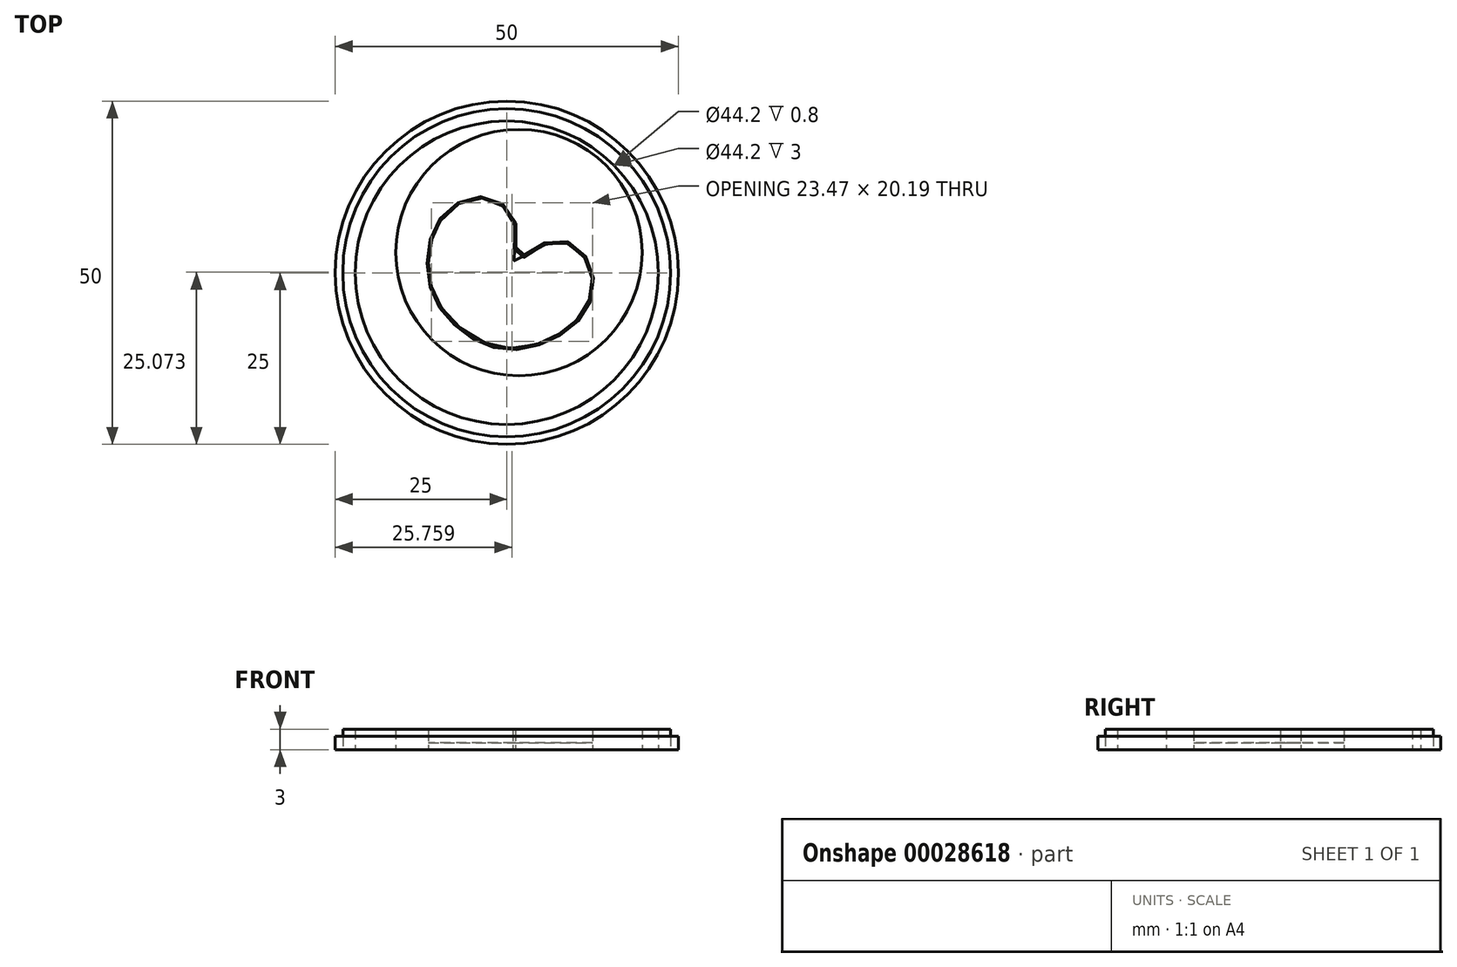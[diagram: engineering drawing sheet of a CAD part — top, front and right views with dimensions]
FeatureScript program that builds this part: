
annotation { "Feature Type Name" : "Feature", "Feature Type Description" : "" }
export const myFeature = defineFeature(function(context is Context, id is Id, definition is map)
    precondition{}
    {
        {
            var Q0;
            Q0=qCreatedBy(makeId("Top.planeOp"),FACE);
            var sketch = newSketch(context, id + "F0", { "sketchPlane" : qUnion([Q0])});
            skCircle(sketch, "E0", {"center": v(0, 0) * mm, "radius": 25 * mm});
            skCircle(sketch, "E1", {"center": v(0, 0) * mm, "radius": 23.9 * mm});
            skCircle(sketch, "E2", {"center": v(0, 0) * mm, "radius": 22.1 * mm});
            skCircle(sketch, "E3", {"center": v(1.78, 2.94) * mm, "radius": 17.95 * mm});
            skPoint(sketch, "E4", {"position": v(0, 25) * mm});
            skPoint(sketch, "E5", {"position": v(0, 20.8) * mm});
            skPoint(sketch, "E6", {"position": v(-15.93, 0) * mm});
            skPoint(sketch, "E7", {"position": v(-25, 0) * mm});
            skLineSegment(sketch, "E8", {"start": v(0.34, 31.79) * mm, "end": v(0.34, -39.78) * mm, "construction": true});
            skPoint(sketch, "E9", {"position": v(0.34, 0) * mm});
            skPoint(sketch, "E10", {"position": v(-3.9, 10.89) * mm});
            skPoint(sketch, "E11", {"position": v(12.51, -1.48) * mm});
            skPoint(sketch, "E12", {"position": v(0.65, -11.01) * mm});
            skPoint(sketch, "E13", {"position": v(-11.43, 1.18) * mm});
            skFitSpline(sketch, "E14", {"points": [v(-10.98, -2) * mm, v(-11.37, -0.01) * mm, v(-11.4, 1.98) * mm, v(-11.15, 3.98) * mm, v(-10.56, 5.9) * mm, v(-10.17, 6.73) * mm, v(-9.73, 7.55) * mm, v(-8.59, 8.96) * mm, v(-6.33, 10.35) * mm, v(-4.5, 10.86) * mm, v(-2.83, 10.77) * mm, v(-1.23, 10.17) * mm, v(0.23, 9.1) * mm, v(0.95, 7.82) * mm, v(1.27, 6.13) * mm, v(1.18, 4) * mm, v(0.99, 2.8) * mm, v(0.86, 2.24) * mm, v(0.93, 1.94) * mm, v(1.1, 1.73) * mm, v(1.55, 1.62) * mm, v(1.95, 1.8) * mm, v(3.45, 2.98) * mm, v(4.68, 3.75) * mm, v(6.04, 4.35) * mm, v(7.5, 4.61) * mm, v(8.89, 4.32) * mm, v(10.24, 3.45) * mm, v(11.54, 2.03) * mm, v(12.21, 0.64) * mm, v(12.5, -1.02) * mm, v(12.48, -2.05) * mm, v(12.07, -3.85) * mm, v(11.28, -5.48) * mm, v(10.26, -6.9) * mm, v(8.96, -8.07) * mm, v(7.48, -9.04) * mm, v(5.93, -9.85) * mm, v(2.94, -10.82) * mm, v(0.92, -11) * mm, v(-1.1, -10.87) * mm, v(-3.45, -10.13) * mm, v(-5.61, -8.95) * mm, v(-8.2, -6.79) * mm, v(-9.57, -5.06) * mm, v(-10.6, -3.07) * mm, v(-10.98, -2) * mm]});
            skLineSegment(sketch, "E15", {"start": v(-11.43, 18.63) * mm, "end": v(-11.43, -20.08) * mm, "construction": true});
            skLineSegment(sketch, "E16", {"start": v(-26.76, 10.89) * mm, "end": v(26.59, 10.89) * mm, "construction": true});
            skLineSegment(sketch, "E17", {"start": v(12.51, 19.74) * mm, "end": v(12.51, -18.58) * mm, "construction": true});
            skLineSegment(sketch, "E18", {"start": v(26.08, -11.01) * mm, "end": v(-24.25, -11.01) * mm, "construction": true});
            skSolve(sketch);
        }
        {
            var Q0;
            Q0=makeQuery(id+"F0.imprint","IMPRINT",FACE,{"disambiguationData":[TD([[makeQuery(id+"F0.imprint","IMPRINT",EDGE,{"derivedFrom":sQuery(id+"F0.wireOp",EDGE,"E0")}),1.0]])]});
            var Q1;
            Q1=makeQuery(id+"F0.imprint","IMPRINT",FACE,{"disambiguationData":[TD([[makeQuery(id+"F0.imprint","IMPRINT",EDGE,{"derivedFrom":sQuery(id+"F0.wireOp",EDGE,"E2")}),1.0]])]});
            extrude(context, id + "F1", {"entities" : qUnion([Q0, Q1]), "depth" : 2 * mm});
        }
        {
            var Q0;
            Q0=makeQuery(id+"F1.opExtrude","CAP_EDGE",EDGE,{"disambiguationData":[OSD([sQuery(id+"F0.wireOp",EDGE,"E0")])],"isStart":true});
            var Q1;
            Q1=makeQuery(id+"F1.opExtrude","CAP_EDGE",EDGE,{"disambiguationData":[OSD([sQuery(id+"F0.wireOp",EDGE,"E1")])],"isStart":true});
            var Q2;
            Q2=makeQuery(id+"F1.opExtrude","CAP_EDGE",EDGE,{"disambiguationData":[OSD([sQuery(id+"F0.wireOp",EDGE,"E2")])],"isStart":true});
            var Q3;
            Q3=makeQuery(id+"F1.opExtrude","CAP_EDGE",EDGE,{"disambiguationData":[OSD([sQuery(id+"F0.wireOp",EDGE,"E3")])],"isStart":true});
            fillet(context, id + "F2", {"entities" : qUnion([Q0, Q1, Q2, Q3]), "radius" : .2 * mm, "tangentPropagation" : true, "allowEdgeOverflow" : false});
        }
        {
            var Q0;
            Q0=makeQuery(id+"F0.imprint","IMPRINT",FACE,{"disambiguationData":[TD([[makeQuery(id+"F0.imprint","IMPRINT",EDGE,{"derivedFrom":sQuery(id+"F0.wireOp",EDGE,"E0")}),1.0]])]});
            extrude(context, id + "F3", {"entities" : qUnion([Q0]), "depth" : 1 * mm});
        }
        {
            var Q0;
            Q0=makeQuery(id+"F0.imprint","IMPRINT",FACE,{"disambiguationData":[TD([[makeQuery(id+"F0.imprint","IMPRINT",EDGE,{"derivedFrom":sQuery(id+"F0.wireOp",EDGE,"E1")}),1.0]])]});
            extrude(context, id + "F4", {"entities" : qUnion([Q0]), "operationType" : NewBodyOperationType.ADD, "depth" : 3 * mm});
        }
        {
            var Q0;
            Q0=makeQuery(id+"F0.imprint","IMPRINT",FACE,{"disambiguationData":[TD([[makeQuery(id+"F0.imprint","IMPRINT",EDGE,{"derivedFrom":sQuery(id+"F0.wireOp",EDGE,"E2")}),1.0]])]});
            extrude(context, id + "F5", {"entities" : qUnion([Q0]), "operationType" : NewBodyOperationType.ADD, "depth" : 1 * mm});
        }
        {
            var Q0;
            Q0=makeQuery(id+"F0.imprint","IMPRINT",FACE,{"disambiguationData":[TD([[makeQuery(id+"F0.imprint","IMPRINT",EDGE,{"derivedFrom":sQuery(id+"F0.wireOp",EDGE,"E3")}),1.0]])]});
            extrude(context, id + "F6", {"entities" : qUnion([Q0]), "operationType" : NewBodyOperationType.ADD, "depth" : 3 * mm});
        }
        {
            var Q0;
            Q0=makeQuery(id+"F0.imprint","IMPRINT",FACE,{"disambiguationData":[TD([[makeQuery(id+"F0.imprint","IMPRINT",EDGE,{"derivedFrom":sQuery(id+"F0.wireOp",EDGE,"E14")}),-1.0]])]});
            extrude(context, id + "F7", {"entities" : qUnion([Q0]), "operationType" : NewBodyOperationType.ADD, "depth" : 1 * mm});
        }
        {
            var Q0;
            Q0=makeQuery(id+"F4.opExtrude","CAP_EDGE",EDGE,{"disambiguationData":[OSD([sQuery(id+"F0.wireOp",EDGE,"E1")])],"isStart":false});
            var Q1;
            Q1=makeQuery(id+"F4.opExtrude","CAP_EDGE",EDGE,{"disambiguationData":[OSD([sQuery(id+"F0.wireOp",EDGE,"E2")])],"isStart":false});
            var Q2;
            Q2=makeQuery(id+"F6.opExtrude","CAP_EDGE",EDGE,{"disambiguationData":[OSD([sQuery(id+"F0.wireOp",EDGE,"E3")])],"isStart":false});
            var Q3;
            Q3=makeQuery(id+"F6.opExtrude","CAP_EDGE",EDGE,{"disambiguationData":[OSD([sQuery(id+"F0.wireOp",EDGE,"E14")])],"isStart":false});
            fillet(context, id + "F8", {"entities" : qUnion([Q0, Q1, Q2, Q3]), "radius" : .2 * mm, "tangentPropagation" : true, "allowEdgeOverflow" : false});
        }
        {
            var Q0;
            Q0=makeQuery(id+"F0.imprint","IMPRINT",FACE,{"disambiguationData":[TD([[makeQuery(id+"F0.imprint","IMPRINT",EDGE,{"derivedFrom":sQuery(id+"F0.wireOp",EDGE,"E3")}),1.0]])]});
            var Q1;
            Q1=makeQuery(id+"F0.imprint","IMPRINT",FACE,{"disambiguationData":[TD([[makeQuery(id+"F0.imprint","IMPRINT",EDGE,{"derivedFrom":sQuery(id+"F0.wireOp",EDGE,"E1")}),1.0]])]});
            extrude(context, id + "F9", {"entities" : qUnion([Q0, Q1]), "depth" : 3 * mm});
        }
    });
